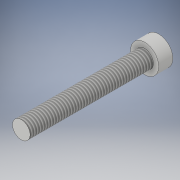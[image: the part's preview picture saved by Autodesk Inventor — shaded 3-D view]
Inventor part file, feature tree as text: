
AUTODESK INVENTOR PART (.ipt)
format: ipt  version: 2018 (Build 220112000, 112)  size: 108,032 bytes
history: native  units: in
note: dims shown in document units (in); Inventor stores cm internally (conversion verified against a paired STEP export)
features: revolve x1, thread x1, sketch x1
ambient origin geometry x8: Origin, YZ Plane, XZ Plane, XY Plane, X Axis, Y Axis, Z Axis, Center Point
bodies: Solid1 (feature_tree)
feature tree (3):
  revolve  "Revolution1"  [1 undecoded]
  thread  "Thread1"  [1 undecoded]
  sketch  "Sketch1"  dims[d0=0.0984in d1=1.378in d2=0.1575in d3=0.1575in d4=90.0deg d5=0.3937in d6=0.0in]
note: 2 required parameter values undecoded (feature->parameter linkage not recoverable at this tier; creation-order binding heuristic only, values carry confidence <= 0.55)